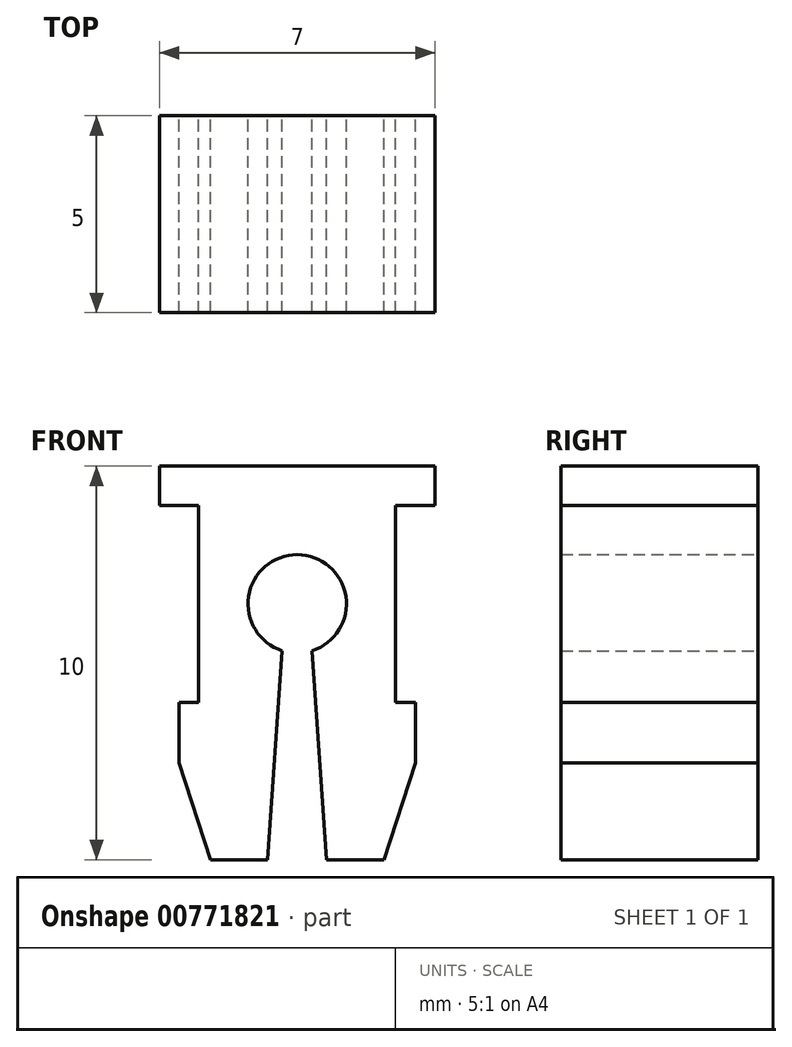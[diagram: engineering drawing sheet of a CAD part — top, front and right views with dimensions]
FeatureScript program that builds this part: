
annotation { "Feature Type Name" : "Feature", "Feature Type Description" : "" }
export const myFeature = defineFeature(function(context is Context, id is Id, definition is map)
    precondition{}
    {
        {
            var Q0;
            Q0=qCreatedBy(makeId("Front.planeOp"),FACE);
            var sketch = newSketch(context, id + "F0", { "sketchPlane" : qUnion([Q0])});
            skLineSegment(sketch, "E0.bottom", {"start": v(-3.5, 3.5) * mm, "end": v(3.5, 3.5) * mm});
            skLineSegment(sketch, "E0.top", {"start": v(-3.5, -6.5) * mm, "end": v(3.5, -6.5) * mm});
            skLineSegment(sketch, "E0.left", {"start": v(-3.5, 3.5) * mm, "end": v(-3.5, -6.5) * mm});
            skLineSegment(sketch, "E0.right", {"start": v(3.5, 3.5) * mm, "end": v(3.5, -6.5) * mm});
            skLineSegment(sketch, "E1.bottom", {"start": v(-3.5, 2.5) * mm, "end": v(-2.5, 2.5) * mm});
            skLineSegment(sketch, "E1.top", {"start": v(-3.5, -2.5) * mm, "end": v(-2.5, -2.5) * mm});
            skLineSegment(sketch, "E1.left", {"start": v(-3.5, 2.5) * mm, "end": v(-3.5, -2.5) * mm});
            skLineSegment(sketch, "E1.right", {"start": v(-2.5, 2.5) * mm, "end": v(-2.5, -2.5) * mm});
            skLineSegment(sketch, "E2.bottom", {"start": v(3.5, -2.5) * mm, "end": v(2.5, -2.5) * mm});
            skLineSegment(sketch, "E2.top", {"start": v(3.5, 2.5) * mm, "end": v(2.5, 2.5) * mm});
            skLineSegment(sketch, "E2.left", {"start": v(3.5, -2.5) * mm, "end": v(3.5, 2.5) * mm});
            skLineSegment(sketch, "E2.right", {"start": v(2.5, -2.5) * mm, "end": v(2.5, 2.5) * mm});
            skCircle(sketch, "E3", {"center": v(0, 0) * mm, "radius": 1.25 * mm});
            skLineSegment(sketch, "E4", {"start": v(-0.38, -1.2) * mm, "end": v(-0.75, -6.5) * mm});
            skLineSegment(sketch, "E5", {"start": v(0.38, -1.2) * mm, "end": v(0.75, -6.5) * mm});
            skLineSegment(sketch, "E6", {"start": v(-3, -2.5) * mm, "end": v(-3, -6.5) * mm});
            skLineSegment(sketch, "E7", {"start": v(3, -2.5) * mm, "end": v(3, -6.5) * mm});
            skLineSegment(sketch, "E8", {"start": v(-3.5, -2.5) * mm, "end": v(-2.2, -6.5) * mm});
            skLineSegment(sketch, "E9", {"start": v(3.5, -2.5) * mm, "end": v(2.2, -6.5) * mm});
            skSolve(sketch);
        }
        {
            var Q0;
            {var subQ7=sQuery(id+"F0.wireOp",EDGE,"E0.bottom");Q0=makeQuery(id+"F0.imprint","IMPRINT",FACE,{"disambiguationData":[TD([[makeQuery(id+"F0.imprint","IMPRINT",EDGE,{"derivedFrom":subQ7}),-1.0]])]});}
            extrude(context, id + "F1", {"entities" : qUnion([Q0]), "depth" : 5 * mm, "offsetDistance" : 25 * mm});
        }
    });
